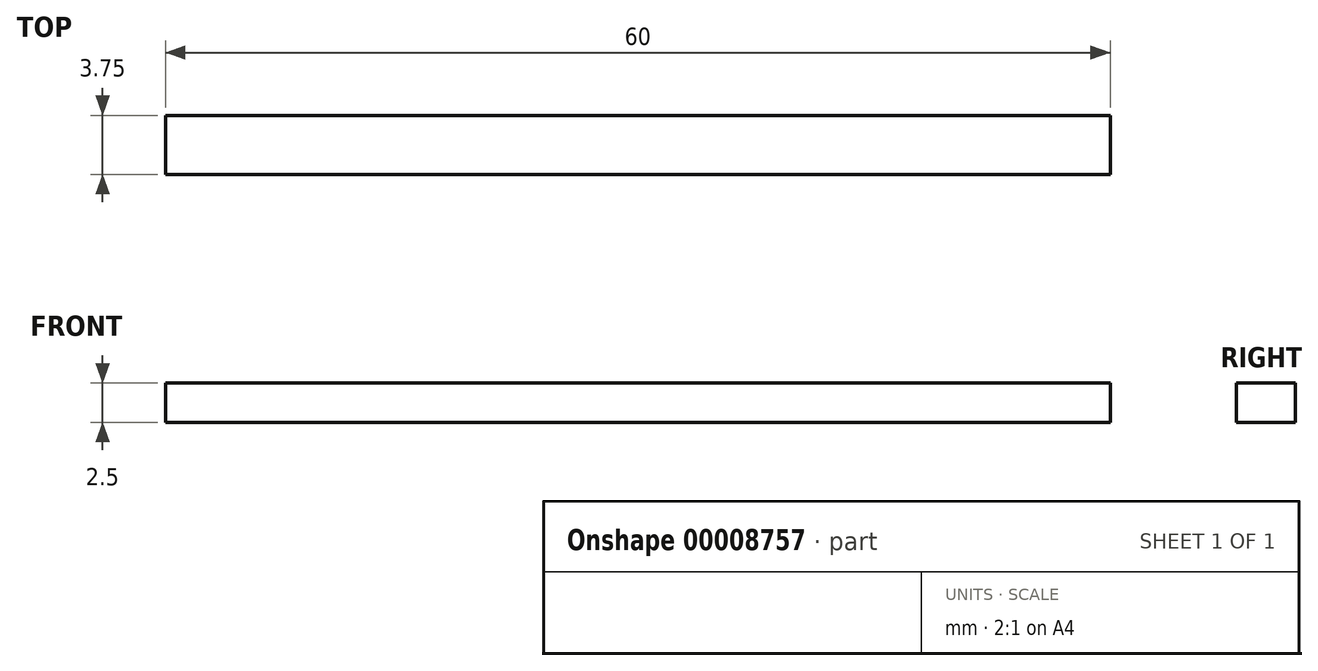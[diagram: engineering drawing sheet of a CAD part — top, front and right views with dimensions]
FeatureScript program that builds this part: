
annotation { "Feature Type Name" : "Feature", "Feature Type Description" : "" }
export const myFeature = defineFeature(function(context is Context, id is Id, definition is map)
    precondition{}
    {
        {
            var Q0;
            Q0=qCreatedBy(makeId("Front.planeOp"),FACE);
            var sketch = newSketch(context, id + "F0", { "sketchPlane" : qUnion([Q0])});
            skLineSegment(sketch, "E0.bottom", {"start": v(7.15, 1.42) * mm, "end": v(67.15, 1.42) * mm});
            skLineSegment(sketch, "E0.top", {"start": v(7.15, -1.08) * mm, "end": v(67.15, -1.08) * mm});
            skLineSegment(sketch, "E0.left", {"start": v(7.15, 1.42) * mm, "end": v(7.15, -1.08) * mm});
            skLineSegment(sketch, "E0.right", {"start": v(67.15, 1.42) * mm, "end": v(67.15, -1.08) * mm});
            skSolve(sketch);
        }
        {
            var Q0;
            Q0 = qSketchRegion(id + "F0", true);
            extrude(context, id + "F1", {"entities" : qUnion([Q0]), "depth" : 3.75 * mm});
        }
    });
